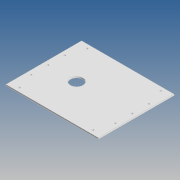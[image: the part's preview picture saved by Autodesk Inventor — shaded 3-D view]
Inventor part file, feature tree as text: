
AUTODESK INVENTOR PART (.ipt)
format: ipt  version: 2020 (Build 240168000, 168)  size: 105,472 bytes
history: native  units: mm
features: other x9, reference x5, extrude x4, sketch x4
ambient origin geometry x8: Origin, YZ Plane, XZ Plane, XY Plane, X Axis, Y Axis, Z Axis, Center Point
bodies: Body1 (feature_tree)
feature tree (22):
  other  "Твердое тело1"
  extrude  "Выдавливание3"  Depth=220.0mm TaperAngle=0.0deg
  extrude  "Выдавливание4"  Depth=3.0mm TaperAngle=0.0deg
  sketch  "Эскиз3"
  reference  "Ссылка1"
  reference  "Ссылка2"
  reference  "Ссылка3"
  reference  "Ссылка4"
  sketch  "Эскиз4"
  reference  "Ссылка5"
  sketch  "Эскиз1"
  sketch  "Эскиз2"
  other  "<path> - Robot.iam"
  other  "000.000 - Robot.iam"
  other  "01_Крепление_мотора:3"
  other  "01_Крепление_мотора:4"
  other  "01_Крепление_мотора:2"
  other  "01_Крепление_мотора:1"
  other  "000.100 - Electronic box:1"
  other  "000.101 - Bottom:1"
  extrude  "Выдавливание1"  Depth=10.0mm TaperAngle=0.0deg
  extrude  "Выдавливание2"  Depth=10.0mm TaperAngle=0.0deg
note: 1 file-system path scrubbed to <path> (originals preserved in map.json)
